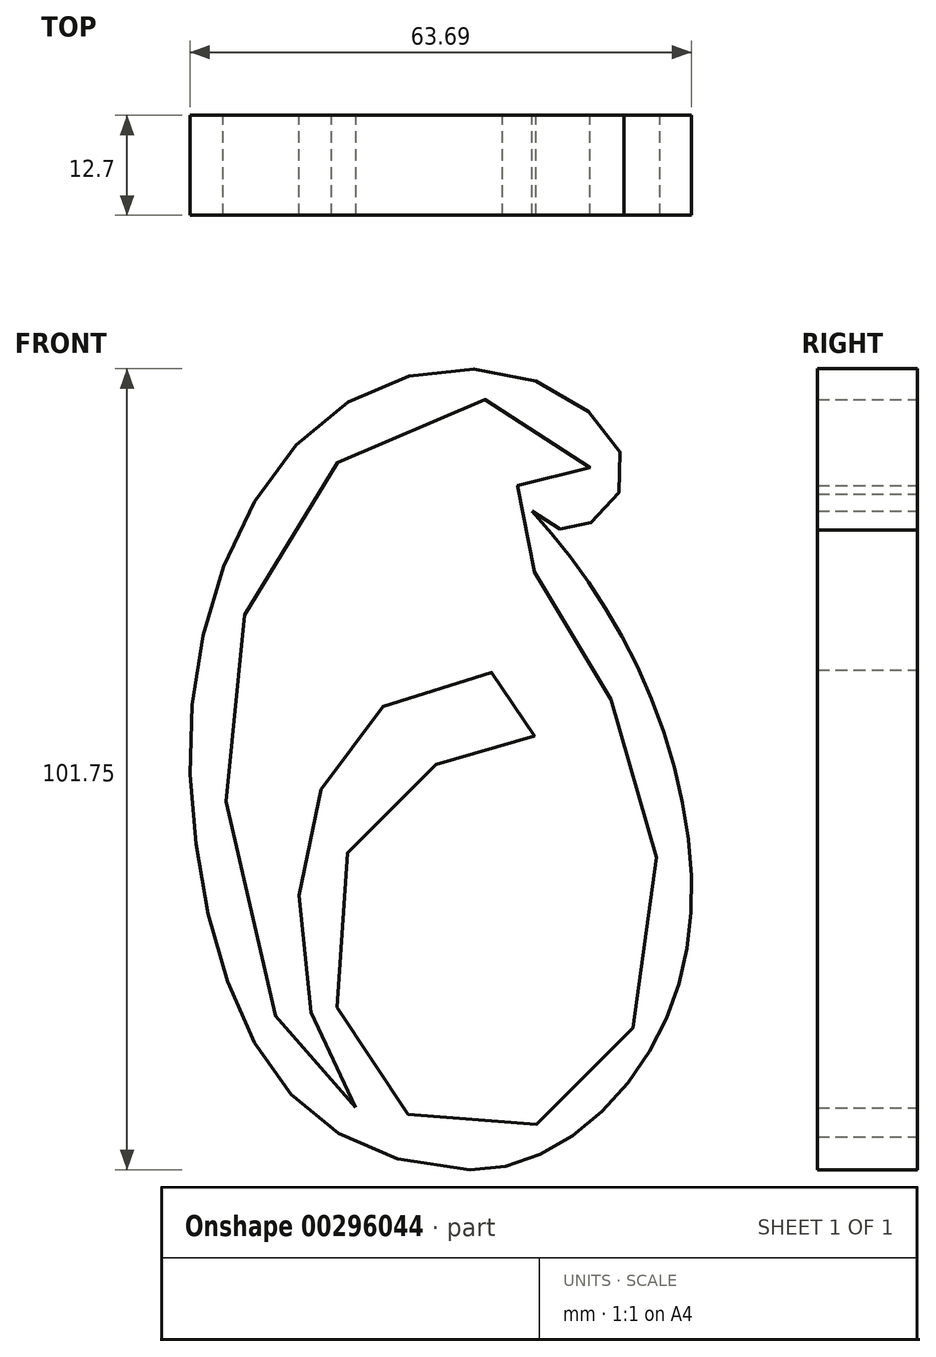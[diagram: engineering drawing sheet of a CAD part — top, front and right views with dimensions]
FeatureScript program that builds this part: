
annotation { "Feature Type Name" : "Feature", "Feature Type Description" : "" }
export const myFeature = defineFeature(function(context is Context, id is Id, definition is map)
    precondition{}
    {
        {
            var Q0;
            Q0=qCreatedBy(makeId("Front.planeOp"),FACE);
            var sketch = newSketch(context, id + "F0", { "sketchPlane" : qUnion([Q0])});
            skFitSpline(sketch, "E0", {"points": [v(0, -47.82) * mm, v(-23.99, -36.77) * mm, v(-34.4, -9.31) * mm, v(-33.46, 21.94) * mm, v(-17.36, 48.45) * mm, v(7.9, 52.55) * mm, v(19.57, 40.56) * mm, v(13.57, 33.61) * mm, v(7.9, 35.82) * mm], "startDerivative": vector(-232.59, 9.34) * mm, "endDerivative": vector(-86.77, 77.7) * mm});
            skFitSpline(sketch, "E1", {"points": [v(0, -47.82) * mm, v(22.72, -32.98) * mm, v(27.77, -6.15) * mm, v(19.57, 19.41) * mm, v(7.9, 35.82) * mm], "startDerivative": vector(105.45, -3.23) * mm, "endDerivative": vector(-58.13, 64.11) * mm});
            skSolve(sketch);
        }
        {
            var Q0;
            Q0=qCreatedBy(makeId("Front.planeOp"),FACE);
            var sketch = newSketch(context, id + "F1", { "sketchPlane" : qUnion([Q0])});
            skFitSpline(sketch, "E2", {"points": [v(-14.52, -39.93) * mm, v(-18.3, -36.77) * mm, v(-23.99, -29.83) * mm, v(-30.3, -6.47) * mm, v(-30.93, 11.84) * mm, v(-25.88, 29.83) * mm, v(-16.73, 42.14) * mm, v(-4.1, 49.08) * mm, v(6.63, 49.4) * mm, v(14.52, 44.03) * mm, v(14.52, 39.3) * mm, v(11.05, 38.03) * mm, v(7.9, 38.66) * mm, v(4.42, 38.66) * mm, v(5.68, 32.04) * mm, v(8.5, 27.59) * mm, v(14.84, 17.53) * mm, v(19.58, 8.03) * mm, v(23.36, -6.15) * mm, v(23.67, -20.04) * mm, v(18, -34.88) * mm, v(11.68, -40.56) * mm, v(3.16, -43.45) * mm, v(-5.71, -42.22) * mm, v(-12.02, -36.49) * mm, v(-16.18, -30.12) * mm, v(-17.4, -15.34) * mm, v(-15.2, -6.76) * mm, v(-10.15, 0) * mm, v(-3.17, 4) * mm, v(4.67, 4.78) * mm, v(7.8, 6.34) * mm, v(8.27, 9.88) * mm, v(6.94, 12.78) * mm, v(3.79, 15) * mm, v(0, 15.62) * mm, v(-7.57, 13.41) * mm, v(-13.57, 8.68) * mm, v(-17.04, 4.58) * mm, v(-19.1, 0) * mm, v(-21, -5.6) * mm, v(-21.67, -10.36) * mm, v(-21.3, -21.25) * mm, v(-20.61, -25.05) * mm, v(-19.74, -30.07) * mm, v(-18.3, -32.98) * mm, v(-14.52, -39.93) * mm]});
            skSolve(sketch);
        }
        {
            var Q0;
            Q0 = qSketchRegion(id + "F0", true);
            var Q1;
            Q1 = qSketchRegion(id + "F1", true);
            extrude(context, id + "F2", {"entities" : qUnion([Q0, Q1]), "depth" : 12.7 * mm});
        }
    });
